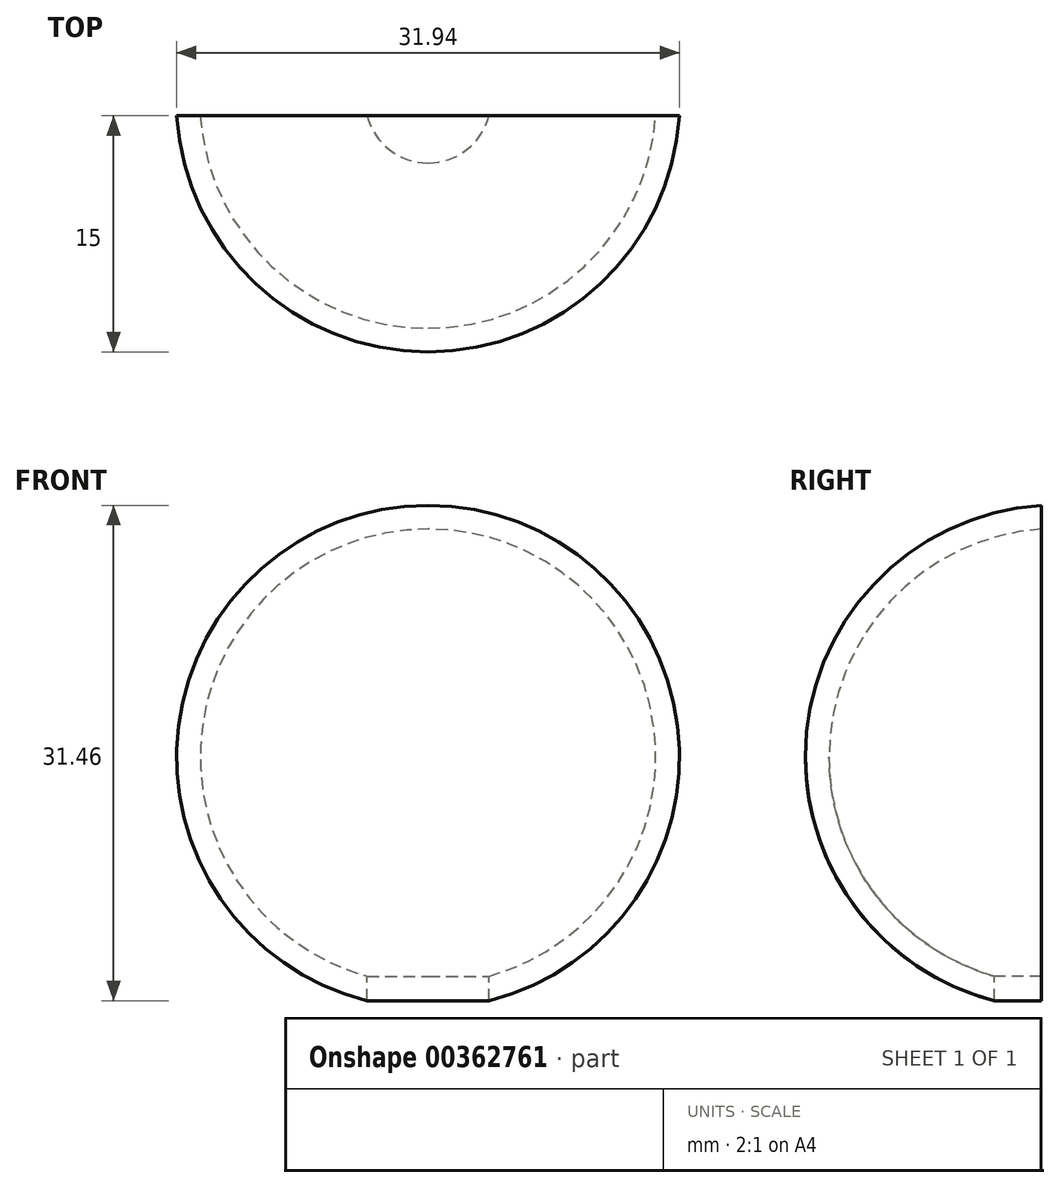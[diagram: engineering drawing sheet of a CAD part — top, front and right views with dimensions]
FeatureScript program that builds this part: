
annotation { "Feature Type Name" : "Feature", "Feature Type Description" : "" }
export const myFeature = defineFeature(function(context is Context, id is Id, definition is map)
    precondition{}
    {
        {
            var Q0;
            Q0=qCreatedBy(makeId("Front.planeOp"),FACE);
            var sketch = newSketch(context, id + "F0", { "sketchPlane" : qUnion([Q0])});
            skCircle(sketch, "E0", {"center": v(0, 0) * mm, "radius": 16 * mm});
            skSolve(sketch);
        }
        {
            var Q0;
            Q0 = qSketchRegion(id + "F0", true);
            extrude(context, id + "F1", {"entities" : qUnion([Q0]), "depth" : 16 * mm});
        }
        {
            var Q0;
            Q0=makeQuery(id+"F1.opExtrude","CAP_EDGE",EDGE,{"disambiguationData":[OSD([sQuery(id+"F0.wireOp",EDGE,"E0")])],"isStart":false});
            fillet(context, id + "F2", {"entities" : qUnion([Q0]), "radius" : 16 * mm, "tangentPropagation" : true, "allowEdgeOverflow" : false});
        }
        {
            var Q0;
            Q0=makeQuery(id+"F1.opExtrude","CAP_FACE",FACE,{"disambiguationData":[OSD([sQuery(id+"F0.wireOp",EDGE,"E0")])],"isStart":true});
            shell(context, id + "F3", {"entities" : qUnion([Q0]), "thickness" : 1.5 * mm});
        }
        {
            var Q0;
            Q0=qCreatedBy(makeId("Top.planeOp"),FACE);
            var sketch = newSketch(context, id + "F4", { "sketchPlane" : qUnion([Q0])});
            skCircle(sketch, "E1", {"center": v(0, 0) * mm, "radius": 4 * mm});
            skSolve(sketch);
        }
        {
            var Q0;
            Q0 = qSketchRegion(id + "F4", true);
            extrude(context, id + "F5", {"entities" : qUnion([Q0]), "operationType" : NewBodyOperationType.REMOVE, "endBound" : BoundingType.THROUGH_ALL, "oppositeDirection" : true, "depth" : 35 * mm});
        }
        {
            var Q0;
            Q0=makeQuery(id+"F1.opExtrude","CAP_FACE",FACE,{"disambiguationData":[OSD([sQuery(id+"F0.wireOp",EDGE,"E0")])],"isStart":true});
            var sketch = newSketch(context, id + "F6", { "sketchPlane" : qUnion([Q0])});
            skLineSegment(sketch, "E2.bottom", {"start": v(-21.02, 20.75) * mm, "end": v(26.82, 20.75) * mm});
            skLineSegment(sketch, "E2.top", {"start": v(-21.02, -26.37) * mm, "end": v(26.82, -26.37) * mm});
            skLineSegment(sketch, "E2.left", {"start": v(-21.02, 20.75) * mm, "end": v(-21.02, -26.37) * mm});
            skLineSegment(sketch, "E2.right", {"start": v(26.82, 20.75) * mm, "end": v(26.82, -26.37) * mm});
            skSolve(sketch);
        }
        {
            var Q0;
            Q0 = qSketchRegion(id + "F6", true);
            extrude(context, id + "F7", {"entities" : qUnion([Q0]), "operationType" : NewBodyOperationType.REMOVE, "oppositeDirection" : true, "depth" : 1 * mm});
        }
    });
